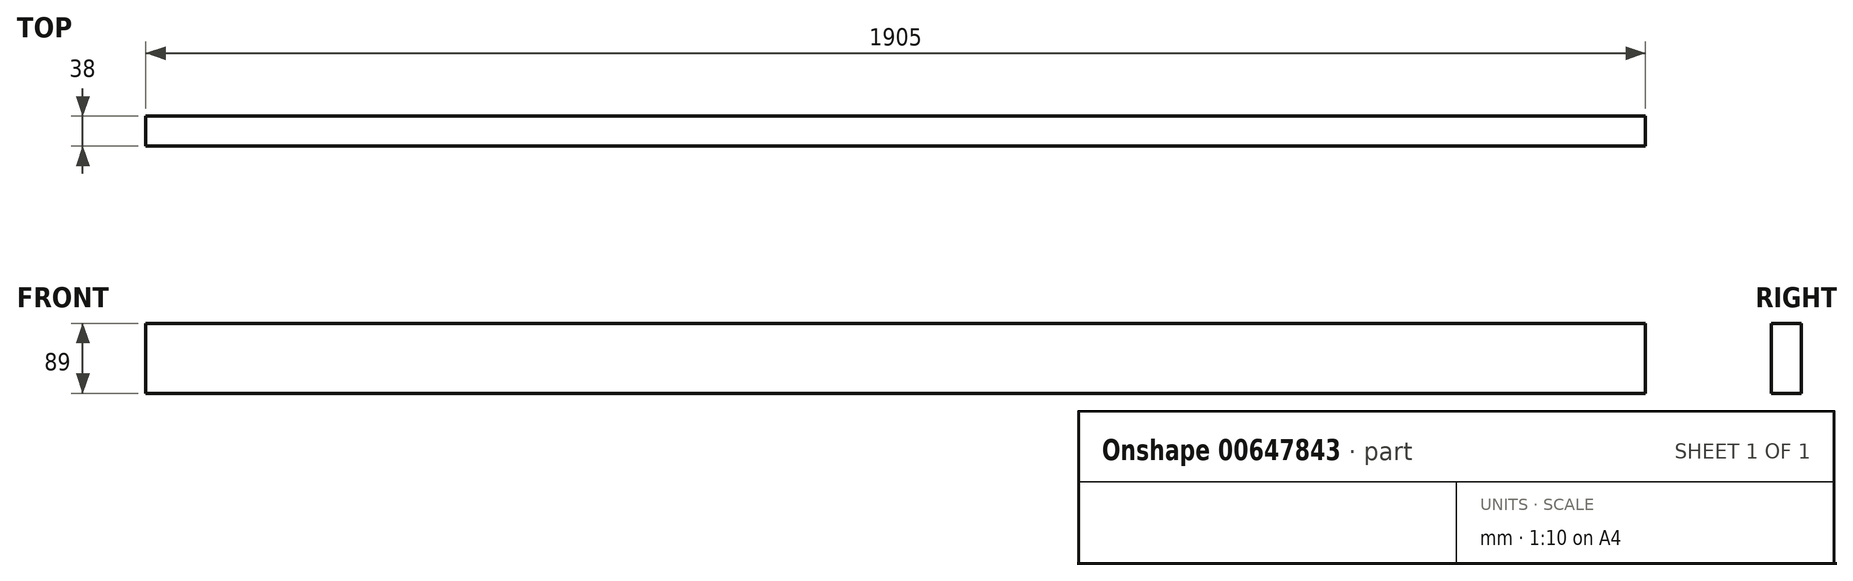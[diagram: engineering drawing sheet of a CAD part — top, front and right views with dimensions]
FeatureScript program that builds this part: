
annotation { "Feature Type Name" : "Feature", "Feature Type Description" : "" }
export const myFeature = defineFeature(function(context is Context, id is Id, definition is map)
    precondition{}
    {
        {
            var Q0;
            Q0=qCreatedBy(makeId("Front.planeOp"),FACE);
            var sketch = newSketch(context, id + "F0", { "sketchPlane" : qUnion([Q0])});
            skLineSegment(sketch, "E0.bottom", {"start": v(-952.5, 44.5) * mm, "end": v(952.5, 44.5) * mm});
            skLineSegment(sketch, "E0.top", {"start": v(-952.5, -44.5) * mm, "end": v(952.5, -44.5) * mm});
            skLineSegment(sketch, "E0.left", {"start": v(-952.5, 44.5) * mm, "end": v(-952.5, -44.5) * mm});
            skLineSegment(sketch, "E0.right", {"start": v(952.5, 44.5) * mm, "end": v(952.5, -44.5) * mm});
            skPoint(sketch, "E0.middle", {"position": v(0, 0) * mm});
            skSolve(sketch);
        }
        {
            var Q0;
            Q0=qSketchRegion(id+"F0",true);
            extrude(context, id + "F1", {"entities" : qUnion([Q0]), "depth" : 38 * mm, "offsetDistance" : 25 * mm});
        }
    });
